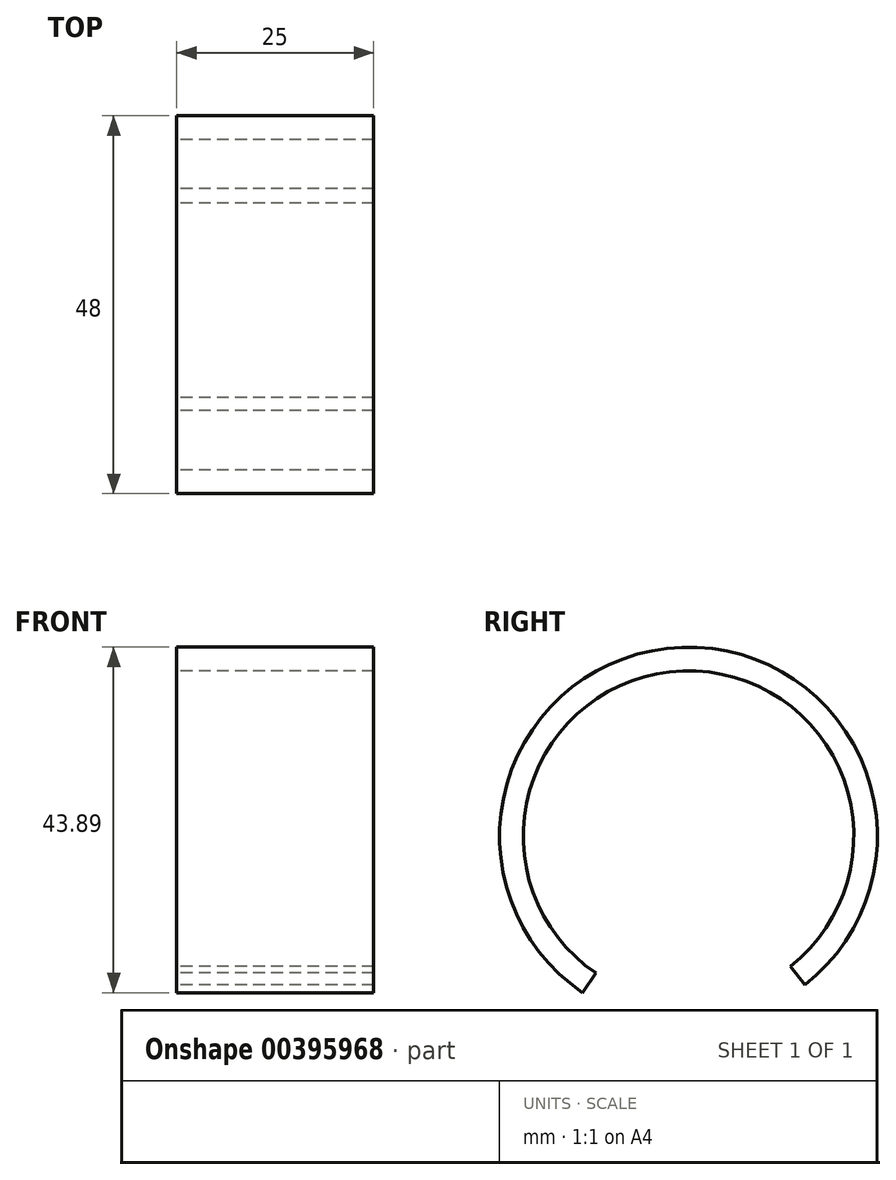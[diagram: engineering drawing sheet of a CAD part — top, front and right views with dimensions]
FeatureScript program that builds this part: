
annotation { "Feature Type Name" : "Feature", "Feature Type Description" : "" }
export const myFeature = defineFeature(function(context is Context, id is Id, definition is map)
    precondition{}
    {
        {
            var Q0;
            Q0=qCreatedBy(makeId("Right.planeOp"),FACE);
            var sketch = newSketch(context, id + "F0", { "sketchPlane" : qUnion([Q0])});
            skArc(sketch, "E0", {"start": v(14.78, -18.91) * mm, "mid": v(-0.83, 23.99) * mm, "end": v(-13.44, -19.89) * mm});
            skArc(sketch, "E1", {"start": v(12.93, -16.55) * mm, "mid": v(-0.73, 20.99) * mm, "end": v(-11.76, -17.4) * mm});
            skLineSegment(sketch, "E2", {"start": v(0, 0) * mm, "end": v(0, -24) * mm});
            skLineSegment(sketch, "E3", {"start": v(-21, 0) * mm, "end": v(-24, 0) * mm});
            skLineSegment(sketch, "E4", {"start": v(21, 0) * mm, "end": v(24, 0) * mm});
            skLineSegment(sketch, "E5", {"start": v(0, 21) * mm, "end": v(0, 24) * mm});
            skLineSegment(sketch, "E6", {"start": v(-13.44, -19.89) * mm, "end": v(0, 0) * mm});
            skLineSegment(sketch, "E7", {"start": v(0, 0) * mm, "end": v(14.78, -18.91) * mm});
            skSolve(sketch);
        }
        {
            var Q0;
            {var subQ0=sQuery(id+"F0.wireOp",EDGE,"E3");Q0=makeQuery(id+"F0.imprint","IMPRINT",FACE,{"disambiguationData":[TD([[makeQuery(id+"F0.imprint","IMPRINT",EDGE,{"derivedFrom":subQ0}),-1.0]])]});}
            var Q1;
            {var subQ3=sQuery(id+"F0.wireOp",EDGE,"E3");Q1=makeQuery(id+"F0.imprint","IMPRINT",FACE,{"disambiguationData":[TD([[makeQuery(id+"F0.imprint","IMPRINT",EDGE,{"derivedFrom":subQ3}),1.0]])]});}
            var Q2;
            {var subQ0=sQuery(id+"F0.wireOp",EDGE,"E4");Q2=makeQuery(id+"F0.imprint","IMPRINT",FACE,{"disambiguationData":[TD([[makeQuery(id+"F0.imprint","IMPRINT",EDGE,{"derivedFrom":subQ0}),1.0]])]});}
            var Q3;
            {var subQ3=sQuery(id+"F0.wireOp",EDGE,"E4");Q3=makeQuery(id+"F0.imprint","IMPRINT",FACE,{"disambiguationData":[TD([[makeQuery(id+"F0.imprint","IMPRINT",EDGE,{"derivedFrom":subQ3}),-1.0]])]});}
            extrude(context, id + "F1", {"entities" : qUnion([Q0, Q1, Q2, Q3]), "depth" : 25 * mm});
        }
    });
